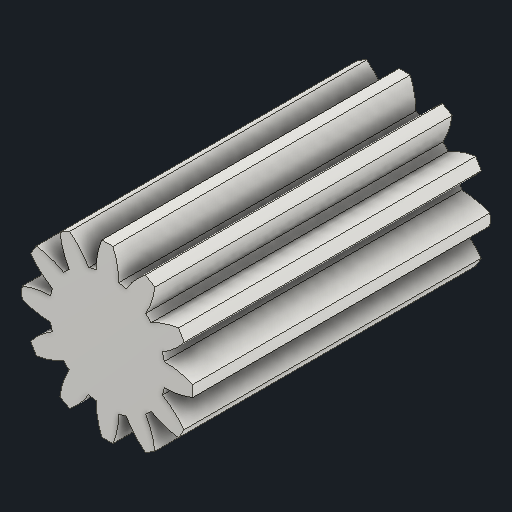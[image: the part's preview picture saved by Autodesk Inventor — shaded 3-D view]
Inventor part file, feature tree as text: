
AUTODESK INVENTOR PART (.ipt)
format: ipt  version: 2024.1 (Build 281209000, 209)  size: 240,128 bytes
history: native  units: mm (DEFAULTED — no unit token found)
features: plane x3, other x3, extrude x1, sketch x1
ambient origin geometry x8: Origin, YZ Plane, XZ Plane, XY Plane, X Axis, Y Axis, Z Axis, Center Point
bodies: Solid1 (feature_tree)
feature tree (8):
  extrude  "Extrusion1"  Depth=18.542mm TaperAngle=0.0deg
  plane  "Work Plane1"
  plane  "Work Plane2"
  plane  "Work Plane3"
  other  "Spur Gear"
  sketch  "Sketch1"  dims[d0=10.668mm d1=18.542mm d2=0.0mm d3=9.144mm d4=76.2mm d5=0.0mm d6=0.0mm d7=15.0deg d9=0.0mm d14=0.0mm d15=23.622mm d16=0.0mm d17=0.0mm d18=0.0mm d19=23.622mm]
  other  "Srf1"
  other  "Pitch Diameter"
